# Revit family: Double C-Channel
name_source: partatom
category: Structural Framing
revit_build: Autodesk Revit Architecture 2012 (Build: 20110210_1515)
units: mm (PartAtom-declared; Revit-internal decimal feet)

## types (93) — shared parameters
Assembly Code = B10

## per-type parameters (varying)
| type | A | Space | W | bf | d | tf | tw |
| 2C15X50 | 29.4 in² | 0' - 0" | 100 | 0' - 3 3/4" | 1' - 3" | 0' - 0 5/8" | 0' - 0 11/16" |
| 2C15X50X.375 | 29.4 in² | 0' - 0 3/8" | 100 | 0' - 3 3/4" | 1' - 3" | 0' - 0 5/8" | 0' - 0 11/16" |
| 2C15X50X.75 | 29.4 in² | 0' - 0 3/4" | 100 | 0' - 3 3/4" | 1' - 3" | 0' - 0 5/8" | 0' - 0 11/16" |
| 2C15X40 | 23.6 in² | 0' - 0" | 80 | 0' - 3 1/2" | 1' - 3" | 0' - 0 5/8" | 0' - 0 1/2" |
| 2C15X40X.375 | 23.6 in² | 0' - 0 3/8" | 80 | 0' - 3 1/2" | 1' - 3" | 0' - 0 5/8" | 0' - 0 1/2" |
| 2C15X40X.75 | 23.6 in² | 0' - 0 3/4" | 80 | 0' - 3 1/2" | 1' - 3" | 0' - 0 5/8" | 0' - 0 1/2" |
| 2C15X33.9 | 20 in² | 0' - 0" | 67.8 | 0' - 3 3/8" | 1' - 3" | 0' - 0 5/8" | 0' - 0 3/8" |
| 2C15X33.9X.375 | 20 in² | 0' - 0 3/8" | 67.8 | 0' - 3 3/8" | 1' - 3" | 0' - 0 5/8" | 0' - 0 3/8" |
| 2C15X33.9X.75 | 20 in² | 0' - 0 3/4" | 67.8 | 0' - 3 3/8" | 1' - 3" | 0' - 0 5/8" | 0' - 0 3/8" |
| 2C12X30 | 17.62 in² | 0' - 0" | 60 | 0' - 3 3/16" | 1' - 0" | 0' - 0 1/2" | 0' - 0 1/2" |
| 2C12X30X.375 | 17.62 in² | 0' - 0 3/8" | 60 | 0' - 3 3/16" | 1' - 0" | 0' - 0 1/2" | 0' - 0 1/2" |
| 2C12X30X.75 | 17.62 in² | 0' - 0 3/4" | 60 | 0' - 3 3/16" | 1' - 0" | 0' - 0 1/2" | 0' - 0 1/2" |
| 2C12X25 | 14.68 in² | 0' - 0" | 50 | 0' - 3 1/16" | 1' - 0" | 0' - 0 1/2" | 0' - 0 3/8" |
| 2C12X25X.375 | 14.68 in² | 0' - 0 3/8" | 50 | 0' - 3 1/16" | 1' - 0" | 0' - 0 1/2" | 0' - 0 3/8" |
| 2C12X25X.75 | 14.68 in² | 0' - 0 3/4" | 50 | 0' - 3 1/16" | 1' - 0" | 0' - 0 1/2" | 0' - 0 3/8" |
| 2C12X20.7 | 12.16 in² | 0' - 0" | 41.4 | 0' - 2 15/16" | 1' - 0" | 0' - 0 1/2" | 0' - 0 5/16" |
| 2C12X20.7X.375 | 12.16 in² | 0' - 0 3/8" | 41.4 | 0' - 2 15/16" | 1' - 0" | 0' - 0 1/2" | 0' - 0 5/16" |
| 2C12X20.7X.75 | 12.16 in² | 0' - 0 3/4" | 41.4 | 0' - 2 15/16" | 1' - 0" | 0' - 0 1/2" | 0' - 0 5/16" |
| 2C10X30 | 17.62 in² | 0' - 0" | 60 | 0' - 3" | 0' - 10" | 0' - 0 7/16" | 0' - 0 11/16" |
| 2C10X30X.375 | 17.62 in² | 0' - 0 3/8" | 60 | 0' - 3" | 0' - 10" | 0' - 0 7/16" | 0' - 0 11/16" |
| 2C10X30X.75 | 17.62 in² | 0' - 0 3/4" | 60 | 0' - 3" | 0' - 10" | 0' - 0 7/16" | 0' - 0 11/16" |
| 2C10X25 | 14.68 in² | 0' - 0" | 50 | 0' - 2 7/8" | 0' - 10" | 0' - 0 7/16" | 0' - 0 1/2" |
| 2C10X25X.375 | 14.68 in² | 0' - 0 3/8" | 50 | 0' - 2 7/8" | 0' - 10" | 0' - 0 7/16" | 0' - 0 1/2" |
| 2C10X25X.75 | 14.68 in² | 0' - 0 3/4" | 50 | 0' - 2 7/8" | 0' - 10" | 0' - 0 7/16" | 0' - 0 1/2" |
| 2C10X20 | 11.74 in² | 0' - 0" | 40 | 0' - 2 3/4" | 0' - 10" | 0' - 0 7/16" | 0' - 0 3/8" |
| 2C10X20X.375 | 11.74 in² | 0' - 0 3/8" | 40 | 0' - 2 3/4" | 0' - 10" | 0' - 0 7/16" | 0' - 0 3/8" |
| 2C10X20X.75 | 11.74 in² | 0' - 0 3/4" | 40 | 0' - 2 3/4" | 0' - 10" | 0' - 0 7/16" | 0' - 0 3/8" |
| 2C10X15.3 | 8.96 in² | 0' - 0" | 30.6 | 0' - 2 5/8" | 0' - 10" | 0' - 0 7/16" | 0' - 0 1/4" |
| 2C10X15.3X.375 | 8.96 in² | 0' - 0 3/8" | 30.6 | 0' - 2 5/8" | 0' - 10" | 0' - 0 7/16" | 0' - 0 1/4" |
| 2C10X15.3X.75 | 8.96 in² | 0' - 0 3/4" | 30.6 | 0' - 2 5/8" | 0' - 10" | 0' - 0 7/16" | 0' - 0 1/4" |
| 2C9X20 | 11.74 in² | 0' - 0" | 40 | 0' - 2 5/8" | 0' - 9" | 0' - 0 7/16" | 0' - 0 7/16" |
| 2C9X20X.375 | 11.74 in² | 0' - 0 3/8" | 40 | 0' - 2 5/8" | 0' - 9" | 0' - 0 7/16" | 0' - 0 7/16" |
| 2C9X20X.75 | 11.74 in² | 0' - 0 3/4" | 40 | 0' - 2 5/8" | 0' - 9" | 0' - 0 7/16" | 0' - 0 7/16" |
| 2C9X15 | 8.82 in² | 0' - 0" | 30 | 0' - 2 1/2" | 0' - 9" | 0' - 0 7/16" | 0' - 0 5/16" |
| 2C9X15X.375 | 8.82 in² | 0' - 0 3/8" | 30 | 0' - 2 1/2" | 0' - 9" | 0' - 0 7/16" | 0' - 0 5/16" |
| 2C9X15X.75 | 8.82 in² | 0' - 0 3/4" | 30 | 0' - 2 1/2" | 0' - 9" | 0' - 0 7/16" | 0' - 0 5/16" |
| 2C9X13.4 | 7.88 in² | 0' - 0" | 26.8 | 0' - 2 7/16" | 0' - 9" | 0' - 0 7/16" | 0' - 0 1/4" |
| 2C9X13.4X.375 | 7.88 in² | 0' - 0 3/8" | 26.8 | 0' - 2 7/16" | 0' - 9" | 0' - 0 7/16" | 0' - 0 1/4" |
| 2C9X13.4X.75 | 7.88 in² | 0' - 0 3/4" | 26.8 | 0' - 2 7/16" | 0' - 9" | 0' - 0 7/16" | 0' - 0 1/4" |
| 2C8X18.7 | 11.02 in² | 0' - 0" | 37.4 | 0' - 2 1/2" | 0' - 8" | 0' - 0 3/8" | 0' - 0 1/2" |
| 2C8X18.7X.375 | 11.02 in² | 0' - 0 3/8" | 37.4 | 0' - 2 1/2" | 0' - 8" | 0' - 0 3/8" | 0' - 0 1/2" |
| 2C8X18.7X.75 | 11.02 in² | 0' - 0 3/4" | 37.4 | 0' - 2 1/2" | 0' - 8" | 0' - 0 3/8" | 0' - 0 1/2" |
| 2C8X13.7 | 8.08 in² | 0' - 0" | 27.4 | 0' - 2 5/16" | 0' - 8" | 0' - 0 3/8" | 0' - 0 5/16" |
| 2C8X13.7X.375 | 8.08 in² | 0' - 0 3/8" | 27.4 | 0' - 2 5/16" | 0' - 8" | 0' - 0 3/8" | 0' - 0 5/16" |
| 2C8X13.7X.75 | 8.08 in² | 0' - 0 3/4" | 27.4 | 0' - 2 5/16" | 0' - 8" | 0' - 0 3/8" | 0' - 0 5/16" |
| 2C8X11.5 | 6.74 in² | 0' - 0" | 23 | 0' - 2 1/4" | 0' - 8" | 0' - 0 3/8" | 0' - 0 1/4" |
| 2C8X11.5X.375 | 6.74 in² | 0' - 0 3/8" | 23 | 0' - 2 1/4" | 0' - 8" | 0' - 0 3/8" | 0' - 0 1/4" |
| 2C8X11.5X.75 | 6.74 in² | 0' - 0 3/4" | 23 | 0' - 2 1/4" | 0' - 8" | 0' - 0 3/8" | 0' - 0 1/4" |
| 2C7X14.7 | 8.66 in² | 0' - 0" | 29.4 | 0' - 2 5/16" | 0' - 7" | 0' - 0 3/8" | 0' - 0 7/16" |
| 2C7X14.7X.375 | 8.66 in² | 0' - 0 3/8" | 29.4 | 0' - 2 5/16" | 0' - 7" | 0' - 0 3/8" | 0' - 0 7/16" |
| 2C7X14.7X.75 | 8.66 in² | 0' - 0 3/4" | 29.4 | 0' - 2 5/16" | 0' - 7" | 0' - 0 3/8" | 0' - 0 7/16" |
| 2C7X12.2 | 7.2 in² | 0' - 0" | 24.4 | 0' - 2 3/16" | 0' - 7" | 0' - 0 3/8" | 0' - 0 5/16" |
| 2C7X12.2X.375 | 7.2 in² | 0' - 0 3/8" | 24.4 | 0' - 2 3/16" | 0' - 7" | 0' - 0 3/8" | 0' - 0 5/16" |
| 2C7X12.2X.75 | 7.2 in² | 0' - 0 3/4" | 24.4 | 0' - 2 3/16" | 0' - 7" | 0' - 0 3/8" | 0' - 0 5/16" |
| 2C7X9.8 | 5.74 in² | 0' - 0" | 19.6 | 0' - 2 1/16" | 0' - 7" | 0' - 0 3/8" | 0' - 0 3/16" |
| 2C7X9.8X.375 | 5.74 in² | 0' - 0 3/8" | 19.6 | 0' - 2 1/16" | 0' - 7" | 0' - 0 3/8" | 0' - 0 3/16" |
| 2C7X9.8X.75 | 5.74 in² | 0' - 0 3/4" | 19.6 | 0' - 2 1/16" | 0' - 7" | 0' - 0 3/8" | 0' - 0 3/16" |
| 2C6X13 | 7.62 in² | 0' - 0" | 26 | 0' - 2 3/16" | 0' - 6" | 0' - 0 5/16" | 0' - 0 7/16" |
| 2C6X13X.375 | 7.62 in² | 0' - 0 3/8" | 26 | 0' - 2 3/16" | 0' - 6" | 0' - 0 5/16" | 0' - 0 7/16" |
| 2C6X13X.75 | 7.62 in² | 0' - 0 3/4" | 26 | 0' - 2 3/16" | 0' - 6" | 0' - 0 5/16" | 0' - 0 7/16" |
| 2C6X10.5 | 6.16 in² | 0' - 0" | 21 | 0' - 2" | 0' - 6" | 0' - 0 5/16" | 0' - 0 5/16" |
| 2C6X10.5X.375 | 6.16 in² | 0' - 0 3/8" | 21 | 0' - 2" | 0' - 6" | 0' - 0 5/16" | 0' - 0 5/16" |
| 2C6X10.5X.75 | 6.16 in² | 0' - 0 3/4" | 21 | 0' - 2" | 0' - 6" | 0' - 0 5/16" | 0' - 0 5/16" |
| 2C6X8.2 | 4.78 in² | 0' - 0" | 16.4 | 0' - 1 15/16" | 0' - 6" | 0' - 0 5/16" | 0' - 0 3/16" |
| 2C6X8.2X.375 | 4.78 in² | 0' - 0 3/8" | 16.4 | 0' - 1 15/16" | 0' - 6" | 0' - 0 5/16" | 0' - 0 3/16" |
| 2C6X8.2X.75 | 4.78 in² | 0' - 0 3/4" | 16.4 | 0' - 1 15/16" | 0' - 6" | 0' - 0 5/16" | 0' - 0 3/16" |
| 2C5X9 | 5.28 in² | 0' - 0" | 18 | 0' - 1 7/8" | 0' - 5" | 0' - 0 5/16" | 0' - 0 5/16" |
| 2C5X9X.375 | 5.28 in² | 0' - 0 3/8" | 18 | 0' - 1 7/8" | 0' - 5" | 0' - 0 5/16" | 0' - 0 5/16" |
| 2C5X9X.75 | 5.28 in² | 0' - 0 3/4" | 18 | 0' - 1 7/8" | 0' - 5" | 0' - 0 5/16" | 0' - 0 5/16" |
| 2C5X6.7 | 3.94 in² | 0' - 0" | 13.4 | 0' - 1 3/4" | 0' - 5" | 0' - 0 5/16" | 0' - 0 3/16" |
| 2C5X6.7X.375 | 3.94 in² | 0' - 0 3/8" | 13.4 | 0' - 1 3/4" | 0' - 5" | 0' - 0 5/16" | 0' - 0 3/16" |
| 2C5X6.7X.75 | 3.94 in² | 0' - 0 3/4" | 13.4 | 0' - 1 3/4" | 0' - 5" | 0' - 0 5/16" | 0' - 0 3/16" |
| 2C4X7.2 | 4.26 in² | 0' - 0" | 14.4 | 0' - 1 3/4" | 0' - 4" | 0' - 0 5/16" | 0' - 0 5/16" |
| 2C4X7.2X.375 | 4.26 in² | 0' - 0 3/8" | 14.4 | 0' - 1 3/4" | 0' - 4" | 0' - 0 5/16" | 0' - 0 5/16" |
| 2C4X7.2X.75 | 4.26 in² | 0' - 0 3/4" | 14.4 | 0' - 1 3/4" | 0' - 4" | 0' - 0 5/16" | 0' - 0 5/16" |
| 2C4X5.4 | 3.16 in² | 0' - 0" | 10.8 | 0' - 1 9/16" | 0' - 4" | 0' - 0 5/16" | 0' - 0 3/16" |
| 2C4X5.4X.375 | 3.16 in² | 0' - 0 3/8" | 10.8 | 0' - 1 9/16" | 0' - 4" | 0' - 0 5/16" | 0' - 0 3/16" |
| 2C4X5.4X.75 | 3.16 in² | 0' - 0 3/4" | 10.8 | 0' - 1 9/16" | 0' - 4" | 0' - 0 5/16" | 0' - 0 3/16" |
| 2C4X4.5 | 2.76 in² | 0' - 0" | 9 | 0' - 1 9/16" | 0' - 4" | 0' - 0 5/16" | 0' - 0 1/8" |
| 2C4X4.5X.375 | 2.76 in² | 0' - 0 3/8" | 9 | 0' - 1 9/16" | 0' - 4" | 0' - 0 5/16" | 0' - 0 1/8" |
| 2C4X4.5X.75 | 2.76 in² | 0' - 0 3/4" | 9 | 0' - 1 9/16" | 0' - 4" | 0' - 0 5/16" | 0' - 0 1/8" |
| 2C3X6 | 3.52 in² | 0' - 0" | 12 | 0' - 1 5/8" | 0' - 3" | 0' - 0 1/4" | 0' - 0 3/8" |
| 2C3X6X.375 | 3.52 in² | 0' - 0 3/8" | 12 | 0' - 1 5/8" | 0' - 3" | 0' - 0 1/4" | 0' - 0 3/8" |
| 2C3X6X.75 | 3.52 in² | 0' - 0 3/4" | 12 | 0' - 1 5/8" | 0' - 3" | 0' - 0 1/4" | 0' - 0 3/8" |
| 2C3X5 | 2.94 in² | 0' - 0" | 10 | 0' - 1 1/2" | 0' - 3" | 0' - 0 1/4" | 0' - 0 1/4" |
| 2C3X5X.375 | 2.94 in² | 0' - 0 3/8" | 10 | 0' - 1 1/2" | 0' - 3" | 0' - 0 1/4" | 0' - 0 1/4" |
| 2C3X5X.75 | 2.94 in² | 0' - 0 3/4" | 10 | 0' - 1 1/2" | 0' - 3" | 0' - 0 1/4" | 0' - 0 1/4" |
| 2C3X4.1 | 2.4 in² | 0' - 0" | 8.2 | 0' - 1 7/16" | 0' - 3" | 0' - 0 1/4" | 0' - 0 3/16" |
| 2C3X4.1X.375 | 2.4 in² | 0' - 0 3/8" | 8.2 | 0' - 1 7/16" | 0' - 3" | 0' - 0 1/4" | 0' - 0 3/16" |
| 2C3X4.1X.75 | 2.4 in² | 0' - 0 3/4" | 8.2 | 0' - 1 7/16" | 0' - 3" | 0' - 0 1/4" | 0' - 0 3/16" |
| 2C3X3.5 | 2.18 in² | 0' - 0" | 7 | 0' - 1 3/8" | 0' - 3" | 0' - 0 1/4" | 0' - 0 1/8" |
| 2C3X3.5X.375 | 2.18 in² | 0' - 0 3/8" | 7 | 0' - 1 3/8" | 0' - 3" | 0' - 0 1/4" | 0' - 0 1/8" |
| 2C3X3.5X.75 | 2.18 in² | 0' - 0 3/4" | 7 | 0' - 1 3/8" | 0' - 3" | 0' - 0 1/4" | 0' - 0 1/8" |

## geometry (parser evidence)
native form markers: Sweep x2
no freeform markers — native parametric forms only
